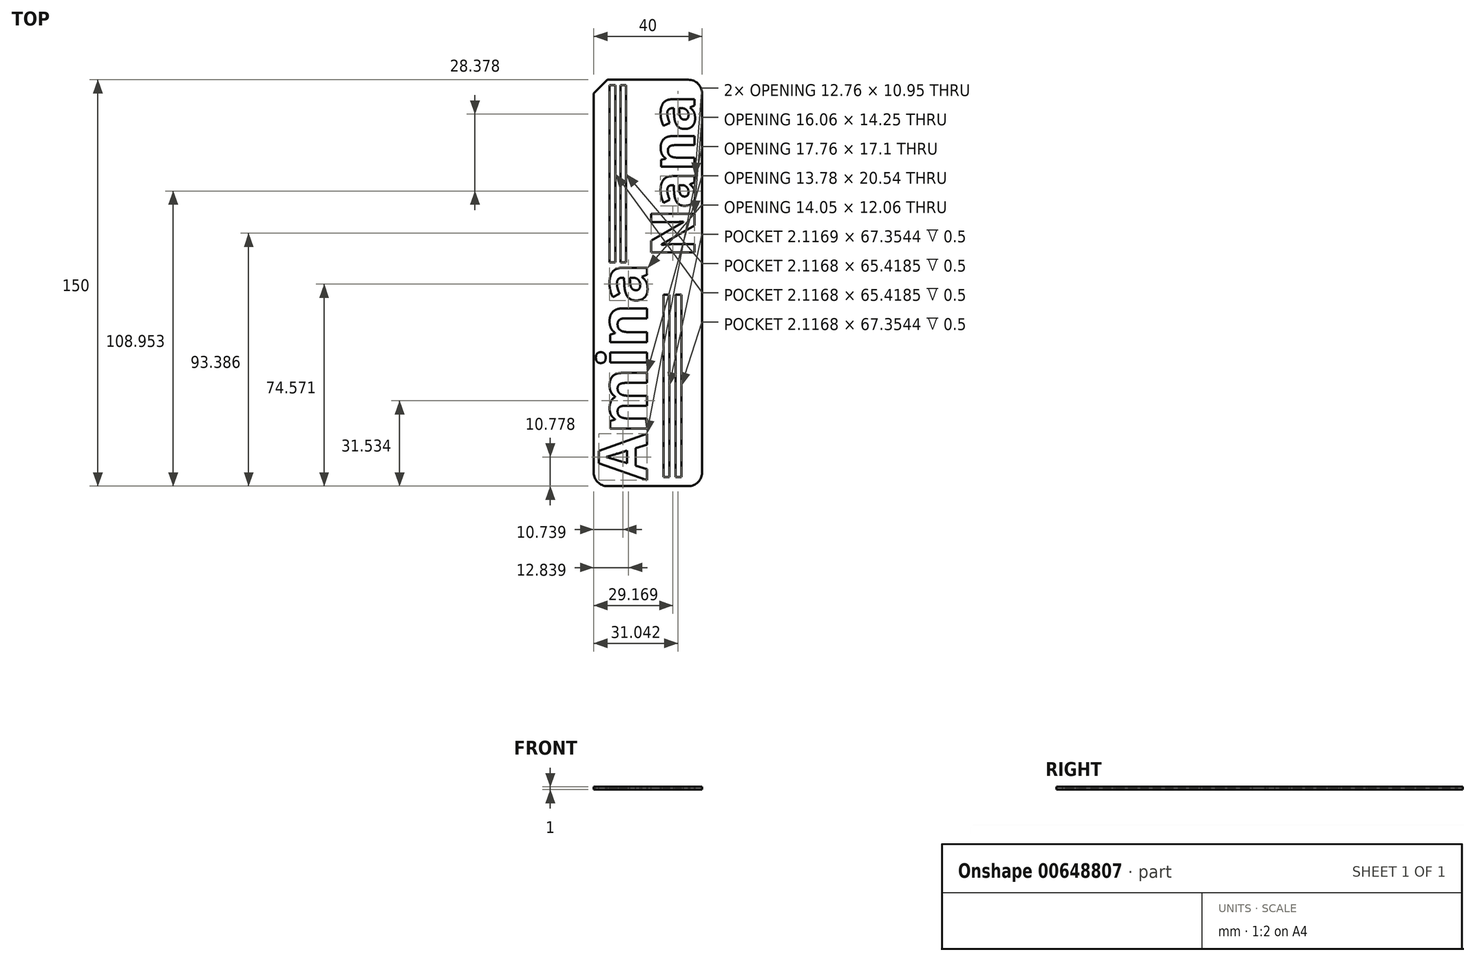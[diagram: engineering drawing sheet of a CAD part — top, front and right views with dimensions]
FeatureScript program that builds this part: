
annotation { "Feature Type Name" : "Feature", "Feature Type Description" : "" }
export const myFeature = defineFeature(function(context is Context, id is Id, definition is map)
    precondition{}
    {
        {
            var Q0;
            Q0=qCreatedBy(makeId("Top.planeOp"),FACE);
            var sketch = newSketch(context, id + "F0", { "sketchPlane" : qUnion([Q0])});
            skLineSegment(sketch, "E0.bottom", {"start": v(-20, 75) * mm, "end": v(20, 75) * mm});
            skLineSegment(sketch, "E0.top", {"start": v(-20, -75) * mm, "end": v(20, -75) * mm});
            skLineSegment(sketch, "E0.left", {"start": v(-20, 75) * mm, "end": v(-20, -75) * mm});
            skLineSegment(sketch, "E0.right", {"start": v(20, 75) * mm, "end": v(20, -75) * mm});
            skPoint(sketch, "E0.middle", {"position": v(0, 0) * mm});
            skSolve(sketch);
        }
        {
            var Q0;
            Q0 = qSketchRegion(id + "F0", true);
            extrude(context, id + "F1", {"entities" : qUnion([Q0]), "depth" : 1 * mm, "offsetDistance" : 25.4 * mm});
        }
        {
            var Q0;
            Q0=makeQuery(id+"F1.opExtrude","CAP_FACE",FACE,{"disambiguationData":[OSD([sQuery(id+"F0.wireOp",EDGE,"E0.bottom"),sQuery(id+"F0.wireOp",EDGE,"E0.top"),sQuery(id+"F0.wireOp",EDGE,"E0.left"),sQuery(id+"F0.wireOp",EDGE,"E0.right")])],"isStart":false});
            var sketch = newSketch(context, id + "F2", { "sketchPlane" : qUnion([Q0])});
            skText(sketch, "E1", { "text": "Amina", "fontName": "OpenSans-Bold.ttf"});
            skText(sketch, "E2", { "text": "Nana", "fontName": "OpenSans-Bold.ttf"});
            const initialGuessF2  = {"E1": [-0.00038, -0.07277, 0, 1, 0.01784], "E2": [0.0172, 0.00924, 0, 1, 0.0162]};
            skSetInitialGuess(sketch, initialGuessF2);
            skSolve(sketch);
        }
        {
            var Q0;
            Q0 = qSketchRegion(id + "F2", true);
            extrude(context, id + "F3", {"entities" : qUnion([Q0]), "operationType" : NewBodyOperationType.REMOVE, "oppositeDirection" : true, "depth" : 25.4 * mm, "offsetDistance" : 25.4 * mm});
        }
        {
            var Q0;
            Q0=makeQuery(id+"F1.opExtrude","SWEPT_EDGE",EDGE,{"disambiguationData":[OSD([sQuery(id+"F0.wireOp",EDGE,"E0.bottom"),sQuery(id+"F0.wireOp",EDGE,"E0.left")])]});
            chamfer(context, id + "F4", {"entities" : qUnion([Q0]), "width" : 5.08 * mm, "tangentPropagation" : true});
        }
        {
            var Q0;
            Q0=makeQuery(id+"F1.opExtrude","SWEPT_EDGE",EDGE,{"disambiguationData":[OSD([sQuery(id+"F0.wireOp",EDGE,"E0.top"),sQuery(id+"F0.wireOp",EDGE,"E0.left")])]});
            var Q1;
            Q1=makeQuery(id+"F1.opExtrude","SWEPT_EDGE",EDGE,{"disambiguationData":[OSD([sQuery(id+"F0.wireOp",EDGE,"E0.top"),sQuery(id+"F0.wireOp",EDGE,"E0.right")])]});
            var Q2;
            Q2=makeQuery(id+"F1.opExtrude","SWEPT_EDGE",EDGE,{"disambiguationData":[OSD([sQuery(id+"F0.wireOp",EDGE,"E0.bottom"),sQuery(id+"F0.wireOp",EDGE,"E0.right")])]});
            fillet(context, id + "F5", {"entities" : qUnion([Q0, Q1, Q2]), "radius" : 5.08 * mm, "tangentPropagation" : true, "allowEdgeOverflow" : false});
        }
        {
            var Q0;
            {var subQ0=sQuery(id+"F0.wireOp",EDGE,"E0.top");var subQ1=sQuery(id+"F0.wireOp",EDGE,"E0.right");var subQ2=sQuery(id+"F0.wireOp",EDGE,"E0.bottom");var subQ3=sQuery(id+"F0.wireOp",EDGE,"E0.left");Q0=makeQuery(id+"F3.boolean.opBoolean","SPLIT",FACE,{"disambiguationData":[TD([makeQuery(id+"F1.opExtrude","SWEPT_FACE",FACE,{"disambiguationData":[OSD([subQ2])]})])],"derivedFrom":makeQuery(id+"F1.opExtrude","CAP_FACE",FACE,{"disambiguationData":[OSD([subQ2,subQ0,subQ3,subQ1])],"isStart":false})});}
            var sketch = newSketch(context, id + "F6", { "sketchPlane" : qUnion([Q0])});
            skLineSegment(sketch, "E3.bottom", {"start": v(5.8, -71.67) * mm, "end": v(7.91, -71.67) * mm});
            skLineSegment(sketch, "E3.top", {"start": v(5.8, -4.31) * mm, "end": v(7.91, -4.31) * mm});
            skLineSegment(sketch, "E3.left", {"start": v(5.8, -71.67) * mm, "end": v(5.8, -4.31) * mm});
            skLineSegment(sketch, "E3.right", {"start": v(7.91, -71.67) * mm, "end": v(7.91, -4.31) * mm});
            skLineSegment(sketch, "E4.bottom", {"start": v(10.19, -71.67) * mm, "end": v(12.3, -71.67) * mm});
            skLineSegment(sketch, "E4.top", {"start": v(10.19, -4.31) * mm, "end": v(12.3, -4.31) * mm});
            skLineSegment(sketch, "E4.left", {"start": v(10.19, -71.67) * mm, "end": v(10.19, -4.31) * mm});
            skLineSegment(sketch, "E4.right", {"start": v(12.3, -71.67) * mm, "end": v(12.3, -4.31) * mm});
            skLineSegment(sketch, "E5.top", {"start": v(-14.16, 72.98) * mm, "end": v(-12.04, 72.98) * mm});
            skLineSegment(sketch, "E5.left", {"start": v(-14.16, 7.56) * mm, "end": v(-14.16, 72.98) * mm});
            skLineSegment(sketch, "E5.right", {"start": v(-12.04, 7.56) * mm, "end": v(-12.04, 72.98) * mm});
            skLineSegment(sketch, "E6", {"start": v(-14.16, 7.56) * mm, "end": v(-12.04, 7.56) * mm});
            skLineSegment(sketch, "E7.top", {"start": v(-10.17, 72.98) * mm, "end": v(-8.05, 72.98) * mm});
            skLineSegment(sketch, "E7.left", {"start": v(-10.17, 7.56) * mm, "end": v(-10.17, 72.98) * mm});
            skLineSegment(sketch, "E7.right", {"start": v(-8.05, 7.56) * mm, "end": v(-8.05, 72.98) * mm});
            skLineSegment(sketch, "E8", {"start": v(-10.17, 7.56) * mm, "end": v(-8.05, 7.56) * mm});
            skSolve(sketch);
        }
        {
            var Q0;
            Q0 = qSketchRegion(id + "F6", true);
            extrude(context, id + "F7", {"entities" : qUnion([Q0]), "operationType" : NewBodyOperationType.REMOVE, "oppositeDirection" : true, "depth" : 0.5 * mm, "offsetDistance" : 25.4 * mm});
        }
    });
